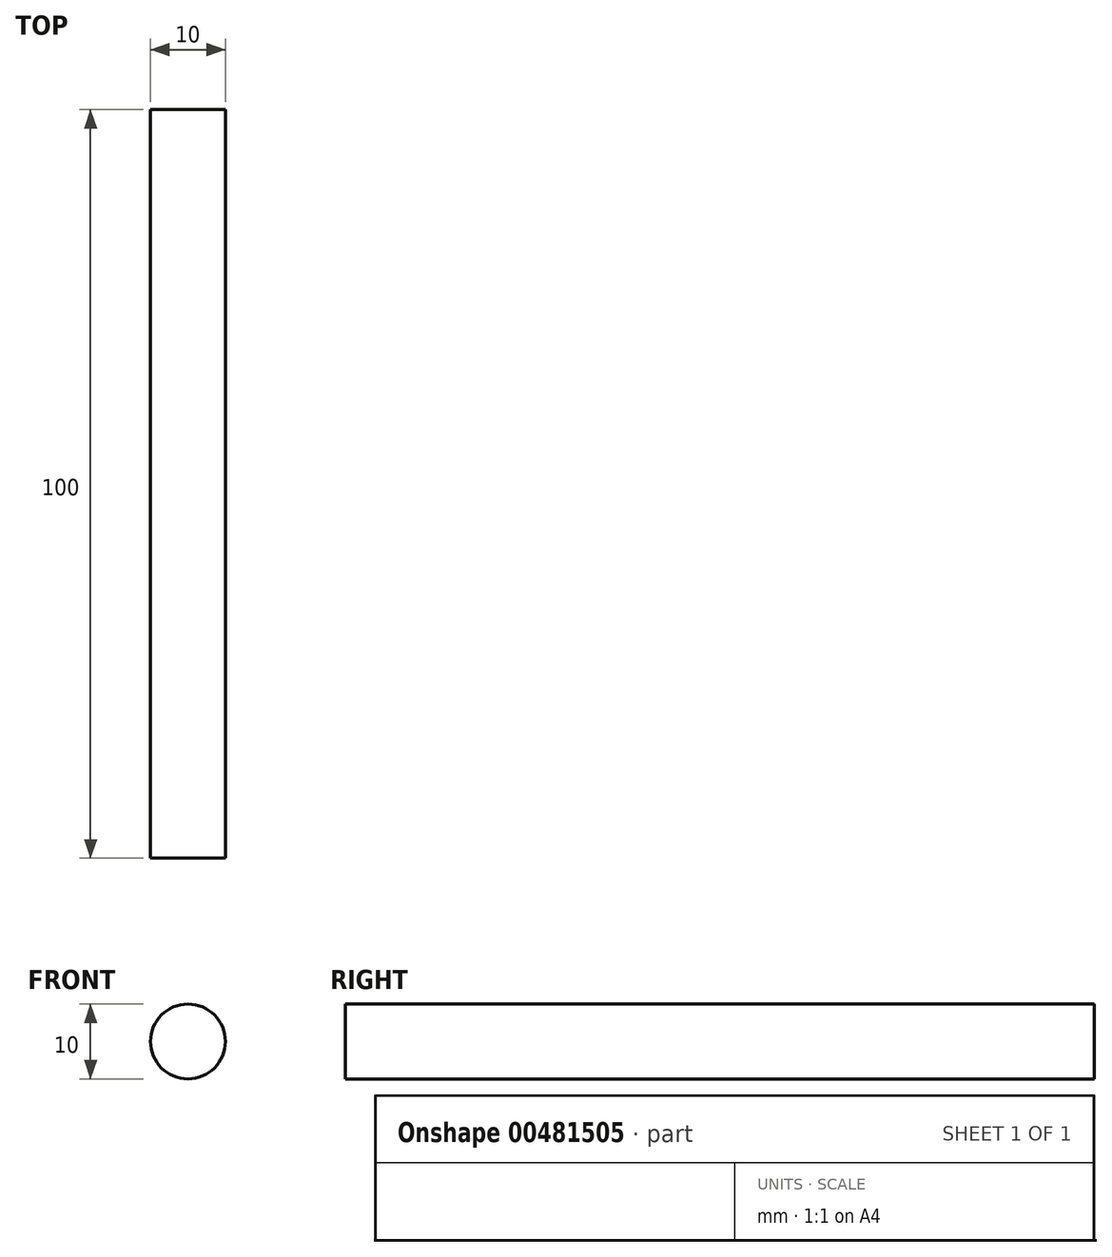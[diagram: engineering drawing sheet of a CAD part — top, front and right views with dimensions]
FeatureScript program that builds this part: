
annotation { "Feature Type Name" : "Feature", "Feature Type Description" : "" }
export const myFeature = defineFeature(function(context is Context, id is Id, definition is map)
    precondition{}
    {
        {
            var Q0;
            Q0=qCreatedBy(makeId("Front.planeOp"),FACE);
            var sketch = newSketch(context, id + "F0", { "sketchPlane" : qUnion([Q0])});
            skCircle(sketch, "E0", {"center": v(0, 0) * mm, "radius": 5 * mm});
            skSolve(sketch);
        }
        {
            var Q0;
            Q0=makeQuery(id+"F0.imprint","IMPRINT",FACE,{"disambiguationData":[TD([[makeQuery(id+"F0.imprint","IMPRINT",EDGE,{"derivedFrom":sQuery(id+"F0.wireOp",EDGE,"E0")}),1.0]])]});
            extrude(context, id + "F1", {"entities" : qUnion([Q0]), "depth" : 100 * mm, "symmetric" : true});
        }
    });
